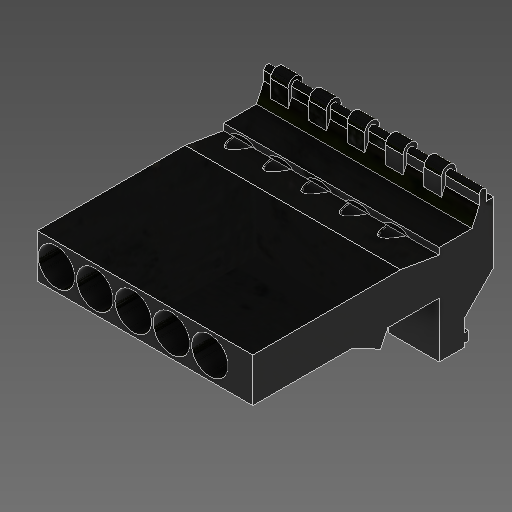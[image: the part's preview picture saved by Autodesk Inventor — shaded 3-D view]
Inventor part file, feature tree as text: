
AUTODESK INVENTOR PART (.ipt)
format: ipt  version: 2020 (Build 240168000, 168)  size: 778,240 bytes
history: native  units: in
note: dims shown in document units (in); Inventor stores cm internally (conversion verified against a paired STEP export)
features: extrude x17, other x15, fillet x3, sketch x3, projected_geometry x3, chamfer x2, pattern_linear x1
ambient origin geometry x8: Origin, YZ Plane, XZ Plane, XY Plane, X Axis, Y Axis, Z Axis, Center Point
bodies: Solid1 (feature_tree)
feature tree (44):
  other  "Base Sketch"
  extrude  "Side Walls"  TaperAngle=0.0deg  [1 undecoded]
  extrude  "Back Wall"  TaperAngle=0.0deg  [1 undecoded]
  extrude  "Front Wall"  Depth=0.0157in
  extrude  "Whistle Housing"  Depth=0.0157in
  extrude  "Tube Socket"  Depth=0.0157in
  other  "Midplane"
  extrude  "Slit"  Depth=0.0157in
  other  "Silicone Fitting"
  extrude  "Silicone Fitting to Chamber"  TaperAngle=90.0deg  [1 undecoded]
  extrude  "Hinge"  Depth=0.0157in TaperAngle=0.0deg
  extrude  "Hinge Nub"  Depth=0.3937in
  chamfer  "Hinge Clearance Chamfer"  [1 undecoded]
  chamfer  "Spring Pass Chamfer"  Distance=0.4331in
  extrude  "Spring Block"  Depth=0.4134in
  extrude  "Spring Hook"  TaperAngle=0.0deg  [1 undecoded]
  other  "Sping Hook Draft"
  fillet  "Spring Hook Fillet"  Radius=0.189in
  extrude  "Edge Cut"  TaperAngle=0.0deg  [1 undecoded]
  fillet  "Edge Fillet"  Radius=0.0079in
  other  "Pincher Triangle Sketch"
  extrude  "Pincher Triangle"  Depth=0.0787in
  extrude  "Triangle Coupling Male"  TaperAngle=45.0deg  [1 undecoded]
  extrude  "Fill: Triangle Coupling Female"  Depth=0.0787in TaperAngle=45.0deg
  pattern_linear  "Key Repitition"  Spacing1=0.2067in  [1 undecoded]
  extrude  "Extrusion28"  Depth=0.0157in
  extrude  "Extrusion29"  Depth=0.0157in
  fillet  "Fillet20"  [1 undecoded]
  sketch  "Sketch5"  dims[d1=0.0in d2=0.0in]
  projected_geometry  "Projected Loop2"
  other  "Whistle Housing Sketch"
  other  "Edge Cut Sketch"
  other  "Slit Sketch"
  other  "Silicone Fitting Sketch"
  other  "Silicone Fitting to Chamber Sketch"
  other  "Tube Socket Sketch"
  other  "Hinge Sketch"
  other  "Hinge Nub Sketch"
  other  "Spring Block Sketch"
  other  "Spring Hook Sketch"
  sketch  "Sketch28"  dims[d3=0.0in d4=0.0in]
  projected_geometry  "Projected Loop4"
  sketch  "Sketch29"  dims[d61=1.5748in d62=0.0in d65=0.0938in d66=0.1181in d67=0.0276in d68=0.0197in d69=90.0deg d71=1.5748in d72=0.0in d78=0.3937in d80=0.0in d81=0.4331in d88=0.4134in d89=0.0in d92=0.189in d93=0.0in d101=0.0079in d105=0.0787in d106=0.1772in d107=45.0deg d112=0.0787in d113=45.0deg d135=0.2067in d136=0.315in d137=0.5906in d139=0.0in d160=0.1181in d161=0.0984in d162=0.3937in d163=0.1575in d164=0.0in d171=1.03in d173=0.4724in d176=0.4134in d177=0.0in d178=0.2067in d179=0.0in d180=0.1374in d181=0.0394in d187=0.2067in d188=0.2362in d190=0.5906in d191=0.0in d193=0.1654in d194=0.0512in d198=0.4134in d199=0.0in d277=0.0079in d278=1.9685in d280=0.4134in d282=0.4134in d283=0.0in d284=0.0394in d285=0.0079in d289=0.0827in d298=0.2067in d299=0.0in d300=0.2559in d301=0.0in d302=0.1969in d303=0.0in d304=0.0787in d305=0.315in d306=0.0079in d307=0.0394in d308=0.0157in]
  projected_geometry  "Projected Loop5"
note: 9 required parameter values undecoded (feature->parameter linkage not recoverable at this tier; creation-order binding heuristic only, values carry confidence <= 0.55)
